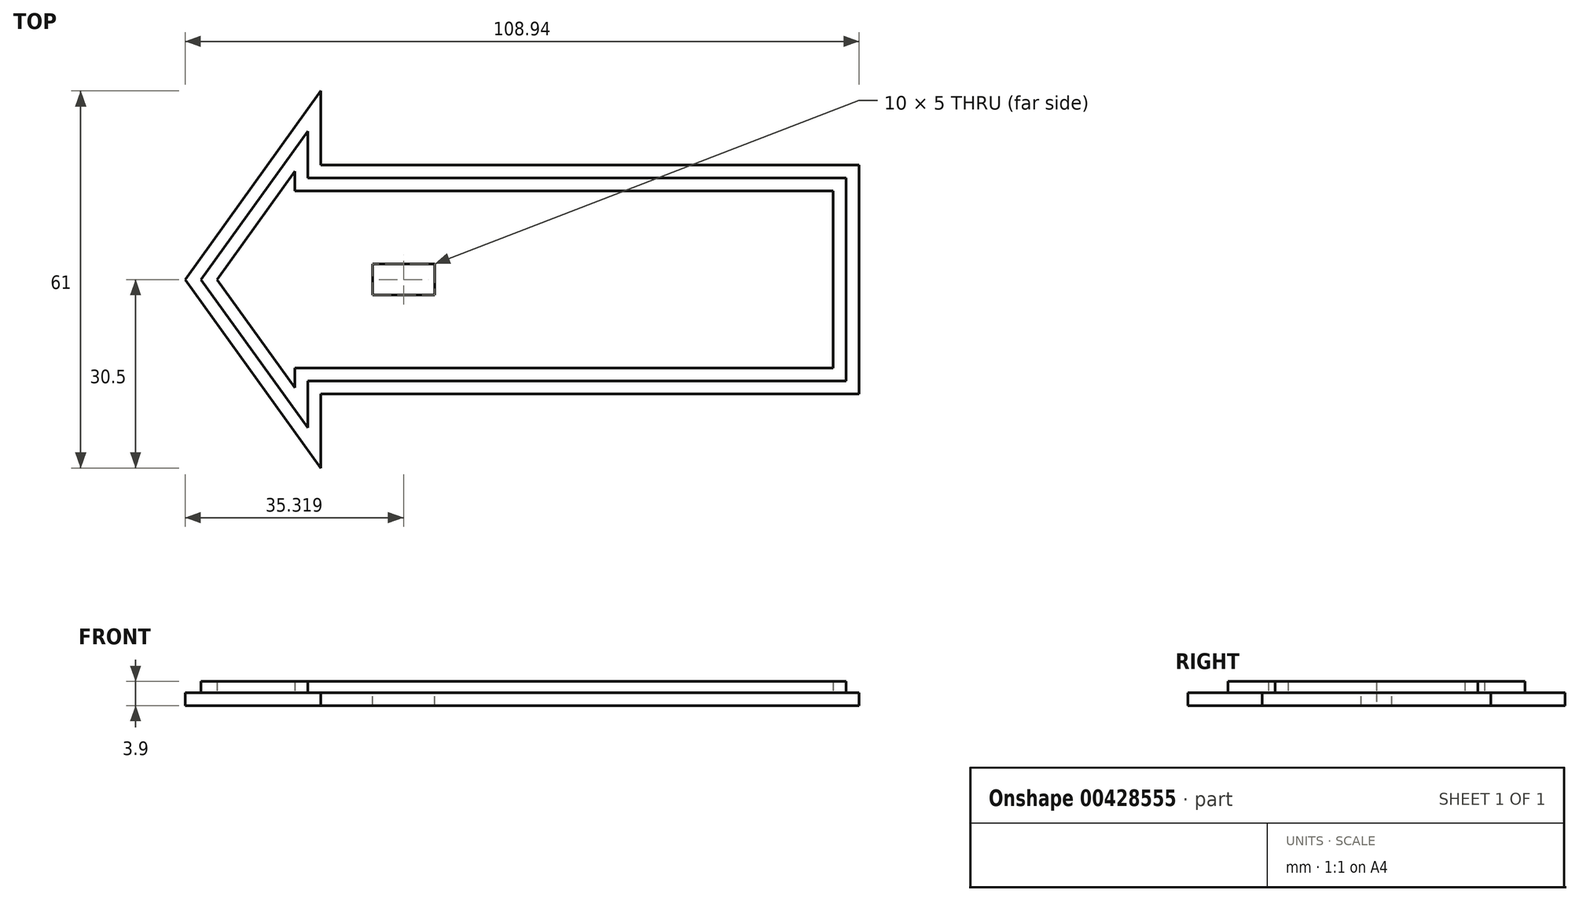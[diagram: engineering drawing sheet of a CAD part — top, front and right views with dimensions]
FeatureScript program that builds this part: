
annotation { "Feature Type Name" : "Feature", "Feature Type Description" : "" }
export const myFeature = defineFeature(function(context is Context, id is Id, definition is map)
    precondition{}
    {
        {
            var Q0;
            Q0=qCreatedBy(makeId("Top.planeOp"),FACE);
            var sketch = newSketch(context, id + "F0", { "sketchPlane" : qUnion([Q0])});
            skLineSegment(sketch, "E0.0", {"start": v(61.6, 18.5) * mm, "end": v(61.6, -18.5) * mm});
            skLineSegment(sketch, "E0.1", {"start": v(-25.4, 18.5) * mm, "end": v(61.6, 18.5) * mm});
            skLineSegment(sketch, "E0.3", {"start": v(-25.4, -18.5) * mm, "end": v(61.6, -18.5) * mm});
            skLineSegment(sketch, "E1", {"start": v(-25.4, 18.5) * mm, "end": v(-25.4, 30.5) * mm});
            skLineSegment(sketch, "E2", {"start": v(-25.4, 30.5) * mm, "end": v(-47.35, 0) * mm});
            skLineSegment(sketch, "E3", {"start": v(-47.35, 0) * mm, "end": v(-25.4, -30.5) * mm});
            skLineSegment(sketch, "E4", {"start": v(-25.4, -30.5) * mm, "end": v(-25.4, -18.5) * mm});
            skPoint(sketch, "E5", {"position": v(61.6, 0) * mm});
            skSolve(sketch);
        }
        {
            var Q0;
            Q0=makeQuery(id+"F0.imprint","IMPRINT",FACE,{"disambiguationData":[TD([[makeQuery(id+"F0.imprint","IMPRINT",EDGE,{"derivedFrom":sQuery(id+"F0.wireOp",EDGE,"E0.0")}),-1.0]])]});
            extrude(context, id + "F1", {"entities" : qUnion([Q0]), "depth" : 2.1 * mm});
        }
        {
            var Q0;
            Q0=makeQuery(id+"F1.opExtrude","CAP_FACE",FACE,{"disambiguationData":[OSD([sQuery(id+"F0.wireOp",EDGE,"E0.0"),sQuery(id+"F0.wireOp",EDGE,"E0.1"),sQuery(id+"F0.wireOp",EDGE,"E0.3"),sQuery(id+"F0.wireOp",EDGE,"E1"),sQuery(id+"F0.wireOp",EDGE,"E2"),sQuery(id+"F0.wireOp",EDGE,"E3"),sQuery(id+"F0.wireOp",EDGE,"E4")])],"isStart":false});
            var sketch = newSketch(context, id + "F2", { "sketchPlane" : qUnion([Q0])});
            skLineSegment(sketch, "E6.0", {"start": v(61.6, 18.5) * mm, "end": v(61.6, -18.5) * mm, "construction": true});
            skLineSegment(sketch, "E6.1", {"start": v(-25.4, 18.5) * mm, "end": v(61.6, 18.5) * mm, "construction": true});
            skLineSegment(sketch, "E6.3", {"start": v(-25.4, -18.5) * mm, "end": v(61.6, -18.5) * mm, "construction": true});
            skLineSegment(sketch, "E7", {"start": v(-25.4, 18.5) * mm, "end": v(-25.4, 30.5) * mm, "construction": true});
            skLineSegment(sketch, "E8", {"start": v(-25.4, 30.5) * mm, "end": v(-47.35, 0) * mm, "construction": true});
            skLineSegment(sketch, "E9", {"start": v(-47.35, 0) * mm, "end": v(-25.4, -30.5) * mm, "construction": true});
            skLineSegment(sketch, "E10", {"start": v(-25.4, -30.5) * mm, "end": v(-25.4, -18.5) * mm, "construction": true});
            skPoint(sketch, "E11", {"position": v(61.6, 0) * mm});
            skLineSegment(sketch, "E12.0", {"start": v(-27.5, 16.4) * mm, "end": v(-27.5, 23.99) * mm});
            skLineSegment(sketch, "E12.1", {"start": v(-27.5, 16.4) * mm, "end": v(59.5, 16.4) * mm});
            skLineSegment(sketch, "E12.2", {"start": v(-44.77, 0) * mm, "end": v(-27.5, -23.99) * mm});
            skLineSegment(sketch, "E12.3", {"start": v(-27.5, -23.99) * mm, "end": v(-27.5, -16.4) * mm});
            skLineSegment(sketch, "E12.4", {"start": v(-27.5, -16.4) * mm, "end": v(59.5, -16.4) * mm});
            skLineSegment(sketch, "E12.5", {"start": v(-27.5, 23.99) * mm, "end": v(-44.77, 0) * mm});
            skLineSegment(sketch, "E12.6", {"start": v(59.5, 16.4) * mm, "end": v(59.5, -16.4) * mm});
            skLineSegment(sketch, "E13.0", {"start": v(-29.6, 14.3) * mm, "end": v(-29.6, 17.47) * mm});
            skLineSegment(sketch, "E13.1", {"start": v(-29.6, 14.3) * mm, "end": v(57.4, 14.3) * mm});
            skLineSegment(sketch, "E13.2", {"start": v(-42.18, 0) * mm, "end": v(-29.6, -17.47) * mm});
            skLineSegment(sketch, "E13.3", {"start": v(-29.6, -17.47) * mm, "end": v(-29.6, -14.3) * mm});
            skLineSegment(sketch, "E13.4", {"start": v(-29.6, -14.3) * mm, "end": v(57.4, -14.3) * mm});
            skLineSegment(sketch, "E13.5", {"start": v(-29.6, 17.47) * mm, "end": v(-42.18, 0) * mm});
            skLineSegment(sketch, "E13.6", {"start": v(57.4, 14.3) * mm, "end": v(57.4, -14.3) * mm});
            skLineSegment(sketch, "E14", {"start": v(59.5, 0) * mm, "end": v(-15, 0) * mm, "construction": true});
            skPoint(sketch, "E14.endSnap0", {"position": v(59.5, 0) * mm});
            skSolve(sketch);
        }
        {
            var Q0;
            Q0=makeQuery(id+"F2.imprint","IMPRINT",FACE,{"disambiguationData":[TD([[makeQuery(id+"F2.imprint","IMPRINT",EDGE,{"derivedFrom":sQuery(id+"F2.wireOp",EDGE,"E12.0")}),1.0]])]});
            extrude(context, id + "F3", {"entities" : qUnion([Q0]), "operationType" : NewBodyOperationType.ADD, "depth" : 1.8 * mm, "offsetDistance" : 25 * mm});
        }
        {
            var Q0;
            Q0=makeQuery(id+"F3.boolean.opBoolean","SPLIT",FACE,{"disambiguationData":[TD([makeQuery(id+"F3.opExtrude","SWEPT_FACE",FACE,{"disambiguationData":[OSD([sQuery(id+"F2.wireOp",EDGE,"E13.0")])]})])],"derivedFrom":makeQuery(id+"F1.opExtrude","CAP_FACE",FACE,{"disambiguationData":[OSD([sQuery(id+"F0.wireOp",EDGE,"E0.0"),sQuery(id+"F0.wireOp",EDGE,"E0.1"),sQuery(id+"F0.wireOp",EDGE,"E0.3"),sQuery(id+"F0.wireOp",EDGE,"E1"),sQuery(id+"F0.wireOp",EDGE,"E2"),sQuery(id+"F0.wireOp",EDGE,"E3"),sQuery(id+"F0.wireOp",EDGE,"E4")])],"isStart":false})});
            var sketch = newSketch(context, id + "F4", { "sketchPlane" : qUnion([Q0])});
            skPoint(sketch, "E15", {"position": v(59.5, 0) * mm});
            skLineSegment(sketch, "E16", {"start": v(59.5, 0) * mm, "end": v(-7.03, 0) * mm, "construction": true});
            skLineSegment(sketch, "E17", {"start": v(-7.03, 0) * mm, "end": v(-7.03, -2.5) * mm});
            skLineSegment(sketch, "E18", {"start": v(-7.03, -2.5) * mm, "end": v(-17.03, -2.5) * mm});
            skLineSegment(sketch, "E19", {"start": v(-17.03, -2.5) * mm, "end": v(-17.03, 2.5) * mm});
            skLineSegment(sketch, "E20", {"start": v(-17.03, 2.5) * mm, "end": v(-7.03, 2.5) * mm});
            skLineSegment(sketch, "E21", {"start": v(-7.03, 2.5) * mm, "end": v(-7.03, 0) * mm});
            skSolve(sketch);
        }
        {
            var Q0;
            Q0=makeQuery(id+"F4.imprint","IMPRINT",FACE,{"disambiguationData":[TD([[makeQuery(id+"F4.imprint","IMPRINT",EDGE,{"derivedFrom":sQuery(id+"F4.wireOp",EDGE,"E17")}),-1.0]])]});
            extrude(context, id + "F5", {"entities" : qUnion([Q0]), "operationType" : NewBodyOperationType.REMOVE, "oppositeDirection" : true, "depth" : 8 * mm, "offsetDistance" : 25 * mm});
        }
    });
